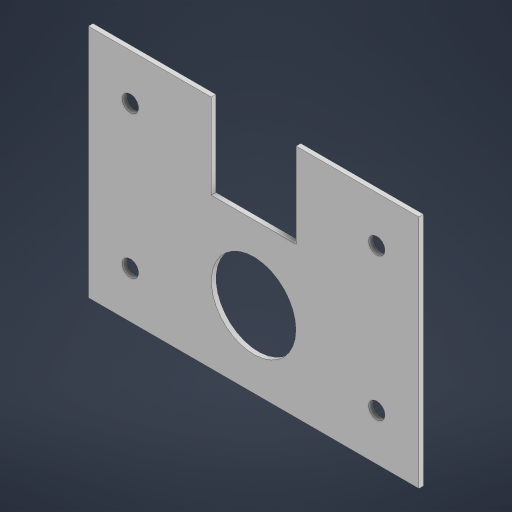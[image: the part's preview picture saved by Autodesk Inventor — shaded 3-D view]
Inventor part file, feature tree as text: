
AUTODESK INVENTOR PART (.ipt)
format: ipt  version: 2024 (Build 280153000, 153)  size: 187,904 bytes
history: native  units: in
note: dims shown in document units (in); Inventor stores cm internally (conversion verified against a paired STEP export)
features: sketch x2, extrude x1, hole x1, mirror x1
ambient origin geometry x8: Origin, YZ Plane, XZ Plane, XY Plane, X Axis, Y Axis, Z Axis, Center Point
bodies: Solid1 (feature_tree)
feature tree (5):
  extrude  "Extrusion1"  Depth=3.13in
  hole  "Hole1"  [1 undecoded]
  mirror  "Mirror1"
  sketch  "Sketch1"  dims[d0=4.4in d1=3.13in]
  sketch  "Sketch2"  dims[d2=1.13in d3=1.13in d4=1.01in d5=1.125in d6=0.0625in d7=0.0in d8=0.217in d9=0.75in d10=0.409in d11=0.25in d12=90.0deg d13=1.0in d14=0.8108in d15=1.9in d16=0.56in d17=0.56in d18=0.62in]
note: 1 required parameter value undecoded (feature->parameter linkage not recoverable at this tier; creation-order binding heuristic only, values carry confidence <= 0.55)
